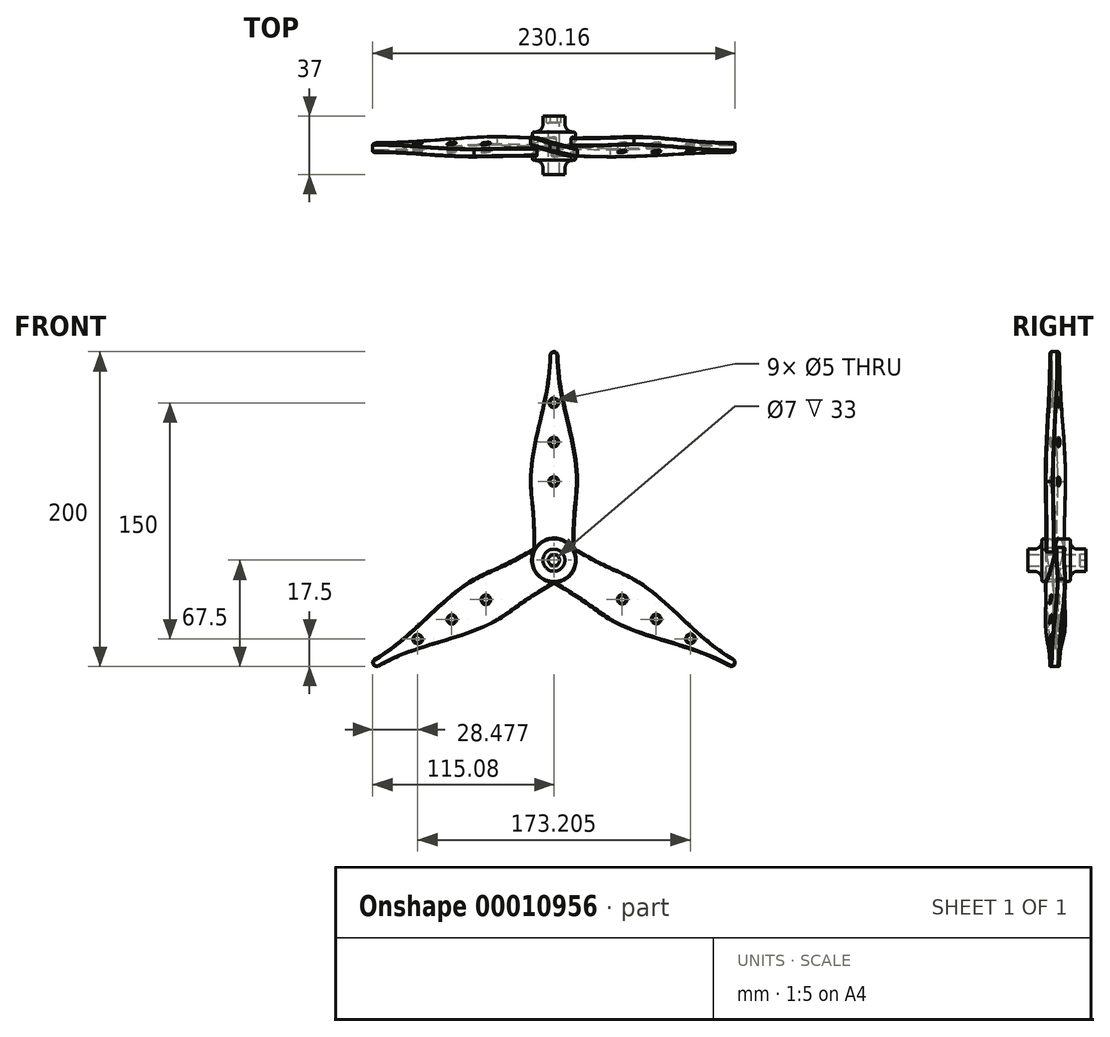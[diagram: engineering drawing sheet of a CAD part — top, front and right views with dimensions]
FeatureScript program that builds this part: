
annotation { "Feature Type Name" : "Feature", "Feature Type Description" : "" }
export const myFeature = defineFeature(function(context is Context, id is Id, definition is map)
    precondition{}
    {
        {
            var Q0;
            Q0=qCreatedBy(makeId("Front.planeOp"),FACE);
            var sketch = newSketch(context, id + "F0", { "sketchPlane" : qUnion([Q0])});
            skCircle(sketch, "E0", {"center": v(0, 0) * mm, "radius": 12.5 * mm});
            skLineSegment(sketch, "E1", {"start": v(0, 0) * mm, "end": v(0, 130) * mm, "construction": true});
            skCircle(sketch, "E2", {"center": v(0, 50) * mm, "radius": 15 * mm});
            skCircle(sketch, "E3", {"center": v(0, 130) * mm, "radius": 2.5 * mm});
            skFitSpline(sketch, "E4", {"points": [v(-15, 50) * mm, v(-2.5, 130) * mm], "startDerivative": vector(0, 77.21) * mm, "endDerivative": vector(0, 83.51) * mm});
            skFitSpline(sketch, "E5", {"points": [v(-15, 50) * mm, v(-12.5, 0) * mm], "startDerivative": vector(2.14, -50) * mm, "endDerivative": vector(0, -100.27) * mm});
            skFitSpline(sketch, "E6.0.MirrorCS", {"points": [v(15, 50) * mm, v(12.5, 0) * mm], "startDerivative": vector(-2.14, -50) * mm, "endDerivative": vector(0, -100.27) * mm});
            skFitSpline(sketch, "E6.1.MirrorCS", {"points": [v(15, 50) * mm, v(2.5, 130) * mm], "startDerivative": vector(0, 77.21) * mm, "endDerivative": vector(0, 83.51) * mm});
            skLineSegment(sketch, "E7.direction2", {"start": v(0, 0) * mm, "end": v(0, 0) * mm});
            skCircle(sketch, "E8", {"center": v(0, 50) * mm, "radius": 2.5 * mm});
            skCircle(sketch, "E9.0.1.0", {"center": v(0, 75) * mm, "radius": 2.5 * mm});
            skCircle(sketch, "E9.0.2.0", {"center": v(0, 100) * mm, "radius": 2.5 * mm});
            skLineSegment(sketch, "E9.direction1", {"start": v(0, 50) * mm, "end": v(0, 50) * mm});
            skLineSegment(sketch, "E9.direction2", {"start": v(0, 50) * mm, "end": v(0, 75) * mm, "construction": true});
            skSolve(sketch);
        }
        {
            var Q0;
            {var subQ1=sQuery(id+"F0.wireOp",EDGE,"E4");Q0=makeQuery(id+"F0.imprint","IMPRINT",FACE,{"disambiguationData":[TD([[makeQuery(id+"F0.imprint","IMPRINT",EDGE,{"derivedFrom":subQ1}),-1.0]])]});}
            var Q1;
            {var subQ1=sQuery(id+"F0.wireOp",EDGE,"E2");var subQ4=sQuery(id+"F0.wireOp",EDGE,"E5");var subQ5=makeQuery(id+"F0.imprint","INTERSECT",VERTEX,{"derivedFrom":[subQ1,subQ4]});Q1=makeQuery(id+"F0.imprint","IMPRINT",FACE,{"disambiguationData":[TD([[makeQuery(id+"F0.imprint","IMPRINT",EDGE,{"disambiguationData":[TD([[subQ5,-1.0]])],"derivedFrom":subQ1}),1.0]])]});}
            var Q2;
            {var subQ3=sQuery(id+"F0.wireOp",EDGE,"E0");var subQ5=sQuery(id+"F0.wireOp",EDGE,"E5");var subQ7=makeQuery(id+"F0.imprint","INTERSECT",VERTEX,{"derivedFrom":[subQ3,subQ5]});Q2=makeQuery(id+"F0.imprint","IMPRINT",FACE,{"disambiguationData":[TD([[makeQuery(id+"F0.imprint","IMPRINT",EDGE,{"disambiguationData":[TD([[subQ7,1.0]])],"derivedFrom":subQ3}),-1.0]])]});}
            var Q3;
            {var subQ0=sQuery(id+"F0.wireOp",EDGE,"E3");var subQ2=makeQuery(id+"F0.imprint","INTERSECT",VERTEX,{"derivedFrom":[subQ0,sQuery(id+"F0.wireOp",EDGE,"E4")]});Q3=makeQuery(id+"F0.imprint","IMPRINT",FACE,{"disambiguationData":[TD([[makeQuery(id+"F0.imprint","IMPRINT",EDGE,{"disambiguationData":[TD([[subQ2,1.0]])],"derivedFrom":subQ0}),1.0]])]});}
            extrude(context, id + "F1", {"entities" : qUnion([Q0, Q1, Q2, Q3]), "depth" : 25 * mm});
        }
        {
            var Q0;
            Q0=qCreatedBy(makeId("Top.planeOp"),FACE);
            var sketch = newSketch(context, id + "F2", { "sketchPlane" : qUnion([Q0])});
            skArc(sketch, "E10", {"start": v(-24.93, 0) * mm, "mid": v(0.22, -8.26) * mm, "end": v(26.12, -13.67) * mm});
            skArc(sketch, "E11", {"start": v(-20.26, -7.1) * mm, "mid": v(4.9, -14.61) * mm, "end": v(30.73, -19.37) * mm});
            skLineSegment(sketch, "E12", {"start": v(30.73, -19.37) * mm, "end": v(26.12, -13.67) * mm});
            skLineSegment(sketch, "E13", {"start": v(-20.26, -7.1) * mm, "end": v(-24.93, 0) * mm});
            skLineSegment(sketch, "E14.bottom", {"start": v(60.99, -43.6) * mm, "end": v(-63.16, -43.6) * mm});
            skLineSegment(sketch, "E14.top", {"start": v(60.99, 26.28) * mm, "end": v(-63.16, 26.28) * mm});
            skLineSegment(sketch, "E14.left", {"start": v(60.99, -43.6) * mm, "end": v(60.99, 26.28) * mm});
            skLineSegment(sketch, "E14.right", {"start": v(-63.16, -43.6) * mm, "end": v(-63.16, 26.28) * mm});
            skSolve(sketch);
        }
        {
            var Q0;
            Q0=makeQuery(id+"F2.imprint","IMPRINT",FACE,{"disambiguationData":[TD([[makeQuery(id+"F2.imprint","IMPRINT",EDGE,{"derivedFrom":sQuery(id+"F2.wireOp",EDGE,"E10")}),1.0]])]});
            extrude(context, id + "F3", {"entities" : qUnion([Q0]), "operationType" : NewBodyOperationType.REMOVE, "endBound" : BoundingType.THROUGH_ALL, "depth" : 25 * mm});
        }
        {
            var Q0;
            Q0=qCreatedBy(makeId("Top.planeOp"),FACE);
            var sketch = newSketch(context, id + "F4", { "sketchPlane" : qUnion([Q0])});
            skLineSegment(sketch, "E15", {"start": v(0, -42.8) * mm, "end": v(0, 37.14) * mm});
            skSolve(sketch);
        }
        {
            var Q0;
            Q0=qCreatedBy(makeId("Right.planeOp"),FACE);
            var sketch = newSketch(context, id + "F5", { "sketchPlane" : qUnion([Q0])});
            skLineSegment(sketch, "E16", {"start": v(37.08, 0) * mm, "end": v(-44.02, 0) * mm, "construction": true});
            skLineSegment(sketch, "E17", {"start": v(9.1, -7) * mm, "end": v(4.1, -7) * mm});
            skLineSegment(sketch, "E18", {"start": v(-0.9, -12) * mm, "end": v(-0.9, -13.6) * mm});
            skLineSegment(sketch, "E19", {"start": v(-0.9, -13.6) * mm, "end": v(-18.9, -13.6) * mm});
            skLineSegment(sketch, "E20", {"start": v(-18.9, -13.6) * mm, "end": v(-18.9, -12) * mm});
            skLineSegment(sketch, "E21", {"start": v(-23.9, -7) * mm, "end": v(-27.9, -7) * mm});
            skPoint(sketch, "E22.visualSharp", {"position": v(-0.9, -7) * mm});
            skArc(sketch, "E22.filletArc", {"start": v(4.1, -7) * mm, "mid": v(0.56, -8.46) * mm, "end": v(-0.9, -12) * mm});
            skPoint(sketch, "E23.visualSharp", {"position": v(-18.9, -7) * mm});
            skArc(sketch, "E23.filletArc", {"start": v(-18.9, -12) * mm, "mid": v(-20.37, -8.46) * mm, "end": v(-23.9, -7) * mm});
            skLineSegment(sketch, "E24", {"start": v(9.1, -7) * mm, "end": v(9.1, -3.5) * mm});
            skLineSegment(sketch, "E25", {"start": v(9.1, -3.5) * mm, "end": v(-27.9, -3.5) * mm});
            skLineSegment(sketch, "E26", {"start": v(-27.9, -3.5) * mm, "end": v(-27.9, -7) * mm});
            skSolve(sketch);
        }
        {
            var Q0;
            Q0=makeQuery(id+"F5.imprint","IMPRINT",FACE,{"disambiguationData":[TD([[makeQuery(id+"F5.imprint","IMPRINT",EDGE,{"derivedFrom":sQuery(id+"F5.wireOp",EDGE,"E17")}),-1.0]])]});
            var Q1;
            Q1=sQuery(id+"F5.wireOp",EDGE,"E16");
            revolve(context, id + "F6", {"operationType" : NewBodyOperationType.ADD, "entities" : qUnion([Q0]), "axis" : qUnion([Q1]), "revolveType" : RevolveType.FULL});
        }
        {
            var Q0;
            Q0=makeQuery(id+"F6.opRevolve","SWEPT_FACE",FACE,{"disambiguationData":[OSD([sQuery(id+"F5.wireOp",EDGE,"E24")])]});
            var sketch = newSketch(context, id + "F7", { "sketchPlane" : qUnion([Q0])});
            skCircle(sketch, "E27.cCircle", {"center": v(0, 0) * mm, "radius": 4 * mm, "construction": true});
            skLineSegment(sketch, "E27.0", {"start": v(-2.3, 4) * mm, "end": v(2.3, 4) * mm});
            skLineSegment(sketch, "E27.1", {"start": v(2.3, 4) * mm, "end": v(4.62, 0) * mm});
            skLineSegment(sketch, "E27.2", {"start": v(4.62, 0) * mm, "end": v(2.3, -4) * mm});
            skLineSegment(sketch, "E27.3", {"start": v(2.3, -4) * mm, "end": v(-2.3, -4) * mm});
            skLineSegment(sketch, "E27.4", {"start": v(-2.3, -4) * mm, "end": v(-4.62, 0) * mm});
            skLineSegment(sketch, "E27.5", {"start": v(-4.62, 0) * mm, "end": v(-2.3, 4) * mm});
            skPoint(sketch, "E27.0.midPoint", {"position": v(0, 4) * mm});
            skSolve(sketch);
        }
        {
            var Q0;
            Q0=makeQuery(id+"F7.imprint","IMPRINT",FACE,{"disambiguationData":[TD([[makeQuery(id+"F7.imprint","IMPRINT",EDGE,{"derivedFrom":sQuery(id+"F7.wireOp",EDGE,"E27.0")}),-1.0]])]});
            var Q1;
            Q1=sQuery(id+"F7.wireOp",EDGE,"E27.cCircle");
            extrude(context, id + "F8", {"entities" : qUnion([Q0]), "operationType" : NewBodyOperationType.REMOVE, "surfaceEntities" : qUnion([Q1]), "oppositeDirection" : true, "depth" : 4 * mm});
        }
        {
            var Q0;
            Q0=makeQuery(id+"F1.opExtrude","SWEPT_BODY",BODY,{"disambiguationData":[OSD([sQuery(id+"F0.wireOp",EDGE,"E0"),sQuery(id+"F0.wireOp",EDGE,"E2"),sQuery(id+"F0.wireOp",EDGE,"E3"),sQuery(id+"F0.wireOp",EDGE,"cf14e29b-c9c8-4d04-a9c3-d7c54be88049"),sQuery(id+"F0.wireOp",EDGE,"7a4d3278-483c-4e90-9639-5dde8eb96df7"),sQuery(id+"F0.wireOp",EDGE,"e3073571-955a-4609-a8b8-91940b3fe371.0.MirrorCS"),sQuery(id+"F0.wireOp",EDGE,"e3073571-955a-4609-a8b8-91940b3fe371.1.MirrorCS")])]});
            var Q1;
            Q1=sQuery(id+"F4.wireOp",EDGE,"E15");
            circularPattern(context, id + "F9", {"operationType" : NewBodyOperationType.ADD, "entities" : qUnion([Q0]), "axis" : qUnion([Q1]), "angle" : 360 * degree, "instanceCount" : 3, "equalSpace" : true});
        }
        {
            var Q0;
            Q0=makeQuery(id+"F6.opRevolve","SWEPT_EDGE",EDGE,{"disambiguationData":[OSD([sQuery(id+"F5.wireOp",EDGE,"E18"),sQuery(id+"F5.wireOp",EDGE,"E19")])]});
            var Q1;
            Q1=makeQuery(id+"F6.opRevolve","SWEPT_EDGE",EDGE,{"disambiguationData":[OSD([sQuery(id+"F5.wireOp",EDGE,"E19"),sQuery(id+"F5.wireOp",EDGE,"E20")])]});
            fillet(context, id + "F10", {"entities" : qUnion([Q0, Q1]), "radius" : 1 * mm, "tangentPropagation" : true, "allowEdgeOverflow" : false});
        }
        {
            var Q0;
            Q0=makeQuery(id+"F3.boolean.opBoolean","COPY",FACE,{"derivedFrom":makeQuery(id+"F3.opExtrude","SWEPT_FACE",FACE,{"disambiguationData":[OSD([sQuery(id+"F2.wireOp",EDGE,"E11")])]})});
            var Q1;
            Q1=makeQuery(id+"F9.opPattern","COPY",FACE,{"derivedFrom":makeQuery(id+"F3.boolean.opBoolean","COPY",FACE,{"derivedFrom":makeQuery(id+"F3.opExtrude","SWEPT_FACE",FACE,{"disambiguationData":[OSD([sQuery(id+"F2.wireOp",EDGE,"E11")])]})}),"instanceName":"2"});
            var Q2;
            Q2=makeQuery(id+"F9.opPattern","COPY",FACE,{"derivedFrom":makeQuery(id+"F3.boolean.opBoolean","COPY",FACE,{"derivedFrom":makeQuery(id+"F3.opExtrude","SWEPT_FACE",FACE,{"disambiguationData":[OSD([sQuery(id+"F2.wireOp",EDGE,"E11")])]})}),"instanceName":"1"});
            var Q3;
            Q3=makeQuery(id+"F9.opPattern","COPY",FACE,{"derivedFrom":makeQuery(id+"F3.boolean.opBoolean","COPY",FACE,{"derivedFrom":makeQuery(id+"F3.opExtrude","SWEPT_FACE",FACE,{"disambiguationData":[OSD([sQuery(id+"F2.wireOp",EDGE,"E10")])]})}),"instanceName":"1"});
            var Q4;
            Q4=makeQuery(id+"F9.opPattern","COPY",FACE,{"derivedFrom":makeQuery(id+"F3.boolean.opBoolean","COPY",FACE,{"derivedFrom":makeQuery(id+"F3.opExtrude","SWEPT_FACE",FACE,{"disambiguationData":[OSD([sQuery(id+"F2.wireOp",EDGE,"E10")])]})}),"instanceName":"2"});
            var Q5;
            Q5=makeQuery(id+"F3.boolean.opBoolean","COPY",FACE,{"derivedFrom":makeQuery(id+"F3.opExtrude","SWEPT_FACE",FACE,{"disambiguationData":[OSD([sQuery(id+"F2.wireOp",EDGE,"E10")])]})});
            fillet(context, id + "F11", {"entities" : qUnion([Q0, Q1, Q2, Q3, Q4, Q5]), "radius" : 0.5 * mm, "tangentPropagation" : true, "allowEdgeOverflow" : false});
        }
    });
